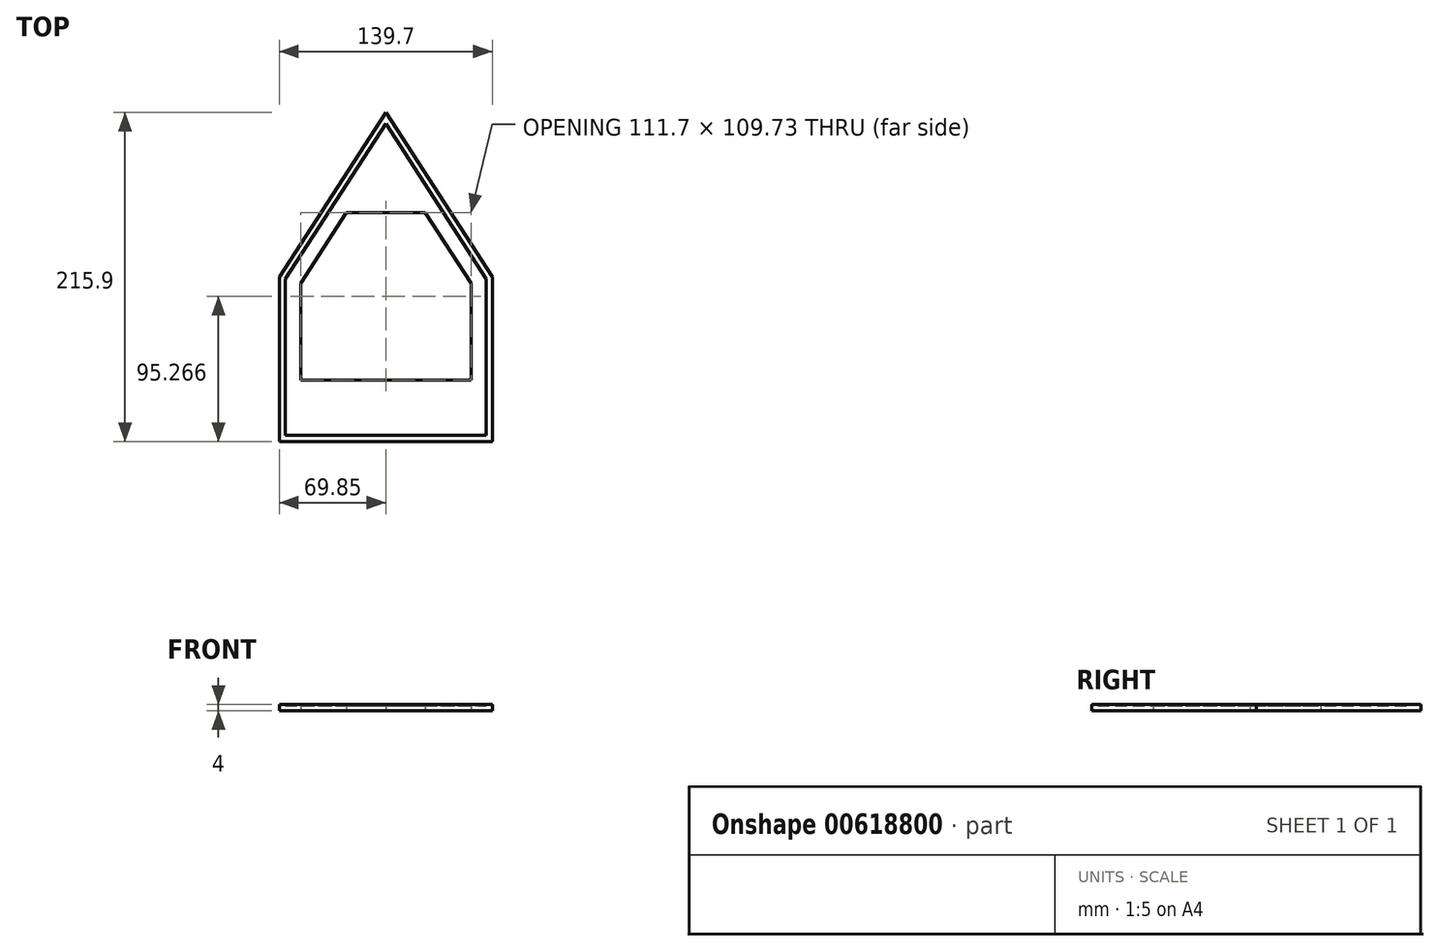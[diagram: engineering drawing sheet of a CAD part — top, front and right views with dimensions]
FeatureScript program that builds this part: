
annotation { "Feature Type Name" : "Feature", "Feature Type Description" : "" }
export const myFeature = defineFeature(function(context is Context, id is Id, definition is map)
    precondition{}
    {
        {
            var Q0;
            Q0=qCreatedBy(makeId("Top.planeOp"),FACE);
            var sketch = newSketch(context, id + "F0", { "sketchPlane" : qUnion([Q0])});
            skLineSegment(sketch, "E0.bottom", {"start": v(69.85, 107.95) * mm, "end": v(-69.85, 107.95) * mm, "construction": true});
            skLineSegment(sketch, "E0.top", {"start": v(69.85, -107.95) * mm, "end": v(-69.85, -107.95) * mm, "construction": true});
            skLineSegment(sketch, "E0.left", {"start": v(69.85, 107.95) * mm, "end": v(69.85, -107.95) * mm, "construction": true});
            skLineSegment(sketch, "E0.right", {"start": v(-69.85, 107.95) * mm, "end": v(-69.85, -107.95) * mm, "construction": true});
            skPoint(sketch, "E0.middle", {"position": v(0, 0) * mm});
            skLineSegment(sketch, "E1.bottom", {"start": v(-69.85, -107.95) * mm, "end": v(69.85, -107.95) * mm});
            skLineSegment(sketch, "E1.top", {"start": v(-69.85, 0) * mm, "end": v(69.85, 0) * mm});
            skLineSegment(sketch, "E1.left", {"start": v(-69.85, -107.95) * mm, "end": v(-69.85, 0) * mm});
            skLineSegment(sketch, "E1.right", {"start": v(69.85, -107.95) * mm, "end": v(69.85, 0) * mm});
            skLineSegment(sketch, "E2", {"start": v(0, 0) * mm, "end": v(0, 107.95) * mm, "construction": true});
            skLineSegment(sketch, "E3", {"start": v(-69.85, 0) * mm, "end": v(0, 107.95) * mm});
            skLineSegment(sketch, "E4", {"start": v(69.85, 0) * mm, "end": v(0, 107.95) * mm});
            skLineSegment(sketch, "E5.0", {"start": v(-65.85, -1.18) * mm, "end": v(0, 100.59) * mm});
            skLineSegment(sketch, "E5.1", {"start": v(65.85, -1.18) * mm, "end": v(0, 100.59) * mm});
            skLineSegment(sketch, "E5.2", {"start": v(-65.85, -103.95) * mm, "end": v(-65.85, -1.18) * mm});
            skLineSegment(sketch, "E5.3", {"start": v(-65.85, -103.95) * mm, "end": v(65.85, -103.95) * mm});
            skLineSegment(sketch, "E5.4", {"start": v(65.85, -103.95) * mm, "end": v(65.85, -1.18) * mm});
            skLineSegment(sketch, "E6.0", {"start": v(55.85, -4.13) * mm, "end": v(0, 82.18) * mm});
            skLineSegment(sketch, "E6.1", {"start": v(-55.85, -4.13) * mm, "end": v(0, 82.18) * mm});
            skLineSegment(sketch, "E6.2", {"start": v(55.85, -93.95) * mm, "end": v(55.85, -4.13) * mm});
            skLineSegment(sketch, "E6.3", {"start": v(-55.85, -93.95) * mm, "end": v(55.85, -93.95) * mm});
            skLineSegment(sketch, "E6.4", {"start": v(-55.85, -93.95) * mm, "end": v(-55.85, -4.13) * mm});
            skPoint(sketch, "E7", {"position": v(0, 42.18) * mm});
            skLineSegment(sketch, "E8", {"start": v(-27.93, 42.18) * mm, "end": v(25.88, 42.18) * mm});
            skPoint(sketch, "E8.startSnap0", {"position": v(-27.93, 39.02) * mm});
            skLineSegment(sketch, "E9", {"start": v(-55.85, -67.55) * mm, "end": v(55.85, -67.55) * mm});
            skSolve(sketch);
        }
        {
            var Q0;
            {var subQ10=sQuery(id+"F0.wireOp",EDGE,"E5.2");Q0=makeQuery(id+"F0.imprint","IMPRINT",FACE,{"disambiguationData":[TD([[makeQuery(id+"F0.imprint","IMPRINT",EDGE,{"derivedFrom":subQ10}),-1.0]])]});}
            var Q1;
            {var subQ0=sQuery(id+"F0.wireOp",EDGE,"E6.3");Q1=makeQuery(id+"F0.imprint","IMPRINT",FACE,{"disambiguationData":[TD([[makeQuery(id+"F0.imprint","IMPRINT",EDGE,{"derivedFrom":subQ0}),1.0]])]});}
            var Q2;
            {var subQ0=sQuery(id+"F0.wireOp",EDGE,"E6.1");var subQ1=sQuery(id+"F0.wireOp",EDGE,"E6.0");var subQ2=makeQuery(id+"F0.imprint","INTERSECT",VERTEX,{"derivedFrom":[subQ1,subQ0]});Q2=makeQuery(id+"F0.imprint","IMPRINT",FACE,{"disambiguationData":[TD([[makeQuery(id+"F0.imprint","IMPRINT",EDGE,{"disambiguationData":[TD([[subQ2,1.0]])],"derivedFrom":subQ1}),1.0]])]});}
            var Q3;
            {var subQ1=sQuery(id+"F0.wireOp",EDGE,"E5.0");var subQ3=sQuery(id+"F0.wireOp",EDGE,"E1.top");var subQ5=makeQuery(id+"F0.imprint","INTERSECT",VERTEX,{"derivedFrom":[subQ3,subQ1]});Q3=makeQuery(id+"F0.imprint","IMPRINT",FACE,{"disambiguationData":[TD([[makeQuery(id+"F0.imprint","IMPRINT",EDGE,{"disambiguationData":[TD([[subQ5,-1.0]])],"derivedFrom":subQ3}),1.0]])]});}
            extrude(context, id + "F1", {"entities" : qUnion([Q0, Q1, Q2, Q3]), "depth" : 3 * mm, "offsetDistance" : 25 * mm});
        }
        {
            var Q0;
            Q0=makeQuery(id+"F0.imprint","IMPRINT",FACE,{"disambiguationData":[TD([[makeQuery(id+"F0.imprint","IMPRINT",EDGE,{"derivedFrom":sQuery(id+"F0.wireOp",EDGE,"E1.bottom")}),1.0]])]});
            var Q1;
            {var subQ1=sQuery(id+"F0.wireOp",EDGE,"E3");Q1=makeQuery(id+"F0.imprint","IMPRINT",FACE,{"disambiguationData":[TD([[makeQuery(id+"F0.imprint","IMPRINT",EDGE,{"derivedFrom":subQ1}),-1.0]])]});}
            extrude(context, id + "F2", {"entities" : qUnion([Q0, Q1]), "operationType" : NewBodyOperationType.ADD, "depth" : 4 * mm, "offsetDistance" : 25 * mm});
        }
    });
